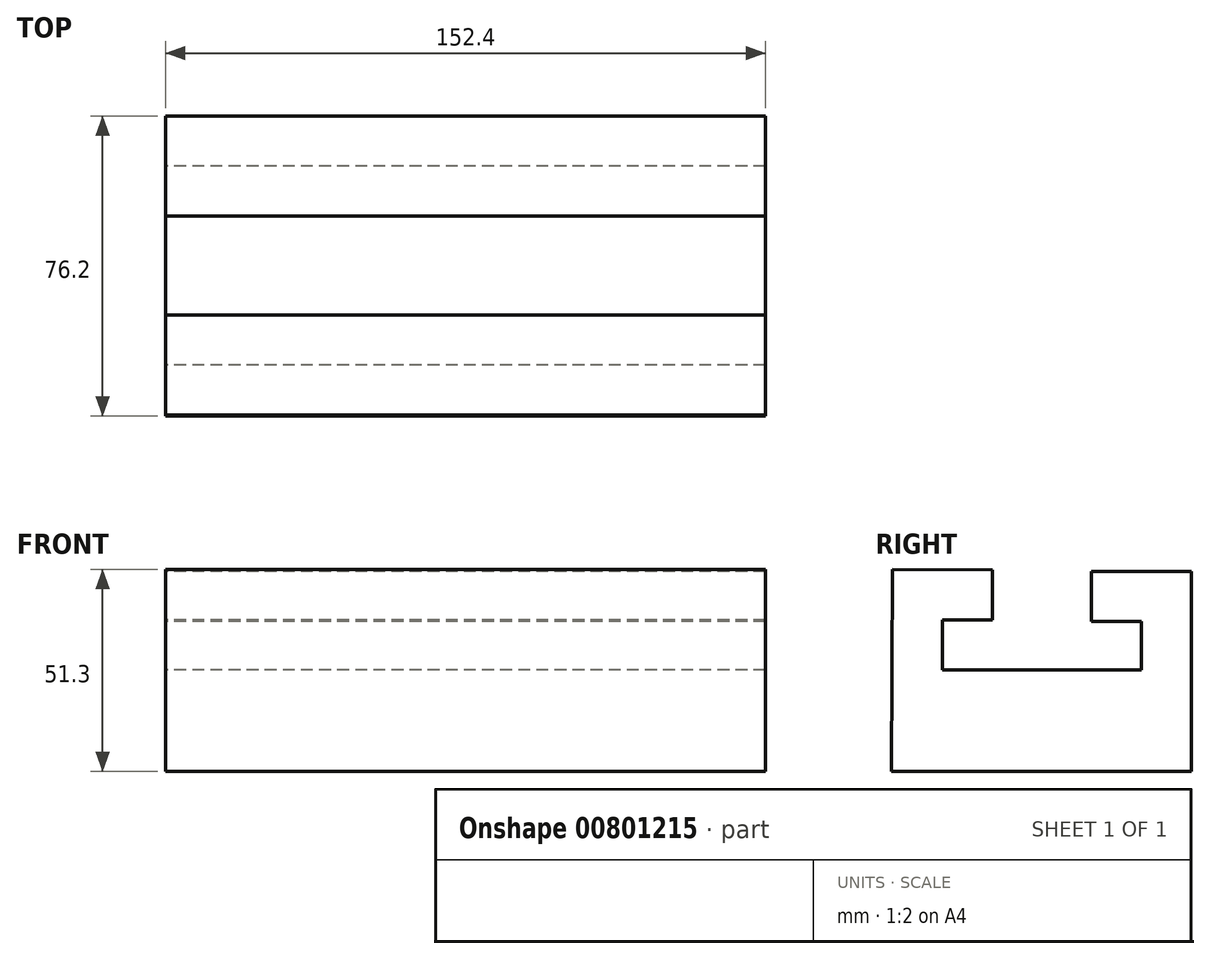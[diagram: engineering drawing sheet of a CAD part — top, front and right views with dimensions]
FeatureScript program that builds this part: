
annotation { "Feature Type Name" : "Feature", "Feature Type Description" : "" }
export const myFeature = defineFeature(function(context is Context, id is Id, definition is map)
    precondition{}
    {
        {
            var Q0;
            Q0=qCreatedBy(makeId("Right.planeOp"),FACE);
            var sketch = newSketch(context, id + "F0", { "sketchPlane" : qUnion([Q0])});
            skLineSegment(sketch, "E0", {"start": v(-47.86, -23.2) * mm, "end": v(28.34, -23.2) * mm});
            skLineSegment(sketch, "E1", {"start": v(28.34, -23.2) * mm, "end": v(28.34, 27.6) * mm});
            skLineSegment(sketch, "E2", {"start": v(28.34, 27.6) * mm, "end": v(2.94, 27.6) * mm});
            skLineSegment(sketch, "E3", {"start": v(2.94, 27.6) * mm, "end": v(2.94, 14.9) * mm});
            skLineSegment(sketch, "E4", {"start": v(2.94, 14.9) * mm, "end": v(15.64, 14.9) * mm});
            skLineSegment(sketch, "E5", {"start": v(15.64, 14.9) * mm, "end": v(15.64, 2.59) * mm});
            skLineSegment(sketch, "E6", {"start": v(15.64, 2.59) * mm, "end": v(-21.7, 2.59) * mm});
            skLineSegment(sketch, "E7", {"start": v(-22.56, 15.29) * mm, "end": v(-22.23, 15.29) * mm});
            skLineSegment(sketch, "E8", {"start": v(-47.63, 28.1) * mm, "end": v(-47.86, -23.2) * mm});
            skLineSegment(sketch, "E9", {"start": v(-47.63, 28.1) * mm, "end": v(-22.23, 27.99) * mm});
            skLineSegment(sketch, "E10", {"start": v(-22.23, 27.99) * mm, "end": v(-22.23, 15.29) * mm});
            skLineSegment(sketch, "E11", {"start": v(-22.23, 15.29) * mm, "end": v(-34.93, 15.29) * mm});
            skLineSegment(sketch, "E12", {"start": v(-34.93, 15.29) * mm, "end": v(-34.93, 2.59) * mm});
            skLineSegment(sketch, "E13", {"start": v(-34.93, 2.59) * mm, "end": v(-21.7, 2.59) * mm});
            skSolve(sketch);
        }
        {
            var Q0;
            Q0 = qSketchRegion(id + "F0", true);
            extrude(context, id + "F1", {"entities" : qUnion([Q0]), "depth" : 152.4 * mm, "offsetDistance" : 25.4 * mm});
        }
    });
